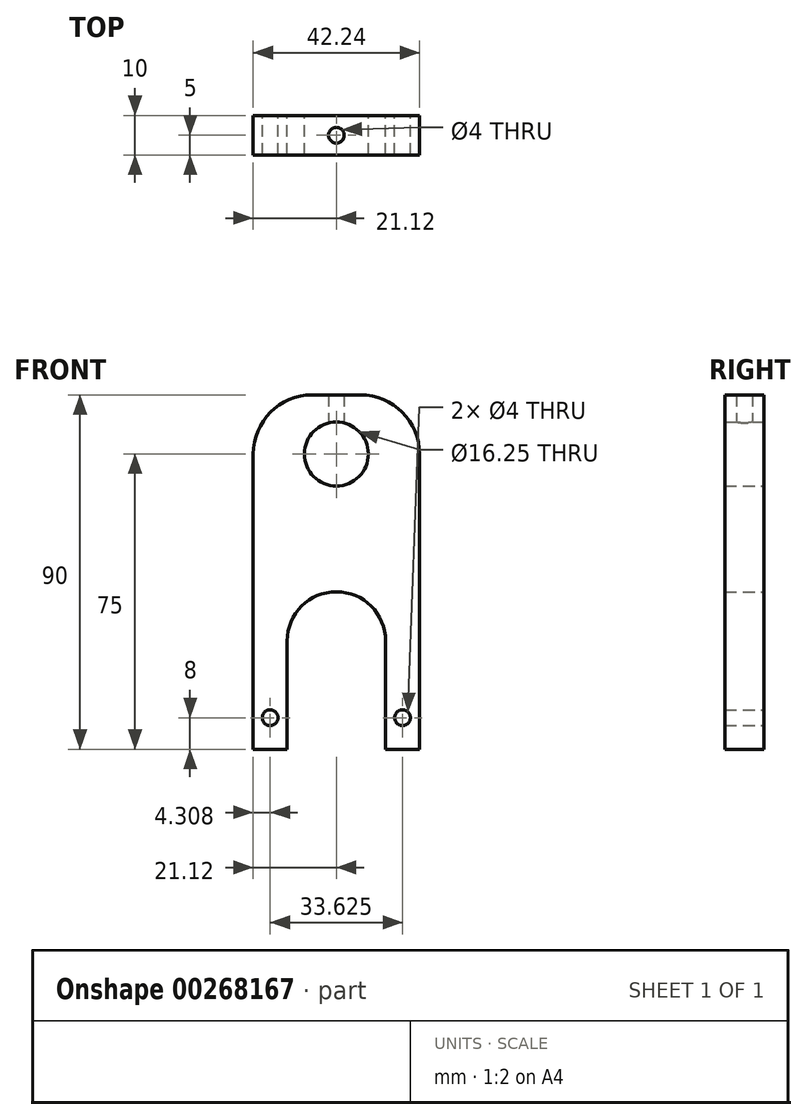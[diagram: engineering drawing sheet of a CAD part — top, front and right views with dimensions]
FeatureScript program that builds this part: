
annotation { "Feature Type Name" : "Feature", "Feature Type Description" : "" }
export const myFeature = defineFeature(function(context is Context, id is Id, definition is map)
    precondition{}
    {
        {
            var Q0;
            Q0=qCreatedBy(makeId("Front.planeOp"),FACE);
            var sketch = newSketch(context, id + "F0", { "sketchPlane" : qUnion([Q0])});
            skLineSegment(sketch, "E0.bottom", {"start": v(6.12, 62.5) * mm, "end": v(-6.13, 62.5) * mm});
            skLineSegment(sketch, "E0.top", {"start": v(21.12, -27.5) * mm, "end": v(12.5, -27.5) * mm});
            skLineSegment(sketch, "E0.left", {"start": v(21.12, 47.5) * mm, "end": v(21.12, -27.5) * mm});
            skLineSegment(sketch, "E0.right", {"start": v(-21.13, 47.5) * mm, "end": v(-21.12, -27.5) * mm});
            skPoint(sketch, "E0.middle", {"position": v(0, 17.5) * mm});
            skLineSegment(sketch, "E1", {"start": v(-12.5, 0) * mm, "end": v(-12.5, -27.5) * mm});
            skLineSegment(sketch, "E2", {"start": v(12.5, 0) * mm, "end": v(12.5, -27.5) * mm});
            skLineSegment(sketch, "E3", {"start": v(-12.5, -27.5) * mm, "end": v(-12.5, -27.5) * mm});
            skLineSegment(sketch, "E4", {"start": v(12.5, -27.5) * mm, "end": v(-12.5, -27.5) * mm, "construction": true});
            skArc(sketch, "E5", {"start": v(-12.5, 0) * mm, "mid": v(0, -12.5) * mm, "end": v(12.5, 0) * mm, "construction": true});
            skArc(sketch, "E6", {"start": v(12.5, 0) * mm, "mid": v(0, 12.5) * mm, "end": v(-12.5, 0) * mm});
            skLineSegment(sketch, "E7", {"start": v(-12.5, -27.5) * mm, "end": v(-21.12, -27.5) * mm});
            skCircle(sketch, "E8", {"center": v(0, 47.5) * mm, "radius": 8.12 * mm});
            skCircle(sketch, "E9", {"center": v(-16.81, -19.5) * mm, "radius": 2 * mm});
            skCircle(sketch, "E10", {"center": v(16.81, -19.5) * mm, "radius": 2 * mm});
            skPoint(sketch, "E11", {"position": v(-16.81, -27.5) * mm});
            skPoint(sketch, "E12", {"position": v(16.81, -27.5) * mm});
            skPoint(sketch, "E13.visualSharp", {"position": v(-21.13, 62.5) * mm});
            skArc(sketch, "E13.filletArc", {"start": v(-6.13, 62.5) * mm, "mid": v(-16.73, 58.1) * mm, "end": v(-21.13, 47.5) * mm});
            skPoint(sketch, "E14.visualSharp", {"position": v(21.12, 62.5) * mm});
            skArc(sketch, "E14.filletArc", {"start": v(21.12, 47.5) * mm, "mid": v(16.73, 58.1) * mm, "end": v(6.13, 62.5) * mm});
            skSolve(sketch);
        }
        {
            var Q0;
            Q0=qCreatedBy(makeId("Top.planeOp"),FACE);
            var sketch = newSketch(context, id + "F1", { "sketchPlane" : qUnion([Q0])});
            skCircle(sketch, "E15", {"center": v(0, 0) * mm, "radius": 2 * mm});
            skCircle(sketch, "E16", {"center": v(-16.81, 0) * mm, "radius": 2 * mm});
            skCircle(sketch, "E17", {"center": v(16.81, 0) * mm, "radius": 2 * mm});
            skLineSegment(sketch, "E18", {"start": v(-21.12, 0) * mm, "end": v(-12.5, 0) * mm, "construction": true});
            skLineSegment(sketch, "E19", {"start": v(12.5, 0) * mm, "end": v(21.12, 0) * mm, "construction": true});
            skSolve(sketch);
        }
        {
            var Q0;
            Q0=makeQuery(id+"F0.imprint","IMPRINT",FACE,{"disambiguationData":[TD([[makeQuery(id+"F0.imprint","IMPRINT",EDGE,{"derivedFrom":sQuery(id+"F0.wireOp",EDGE,"E0.bottom")}),1.0]])]});
            extrude(context, id + "F2", {"entities" : qUnion([Q0]), "endBound" : BoundingType.SYMMETRIC, "depth" : 10 * mm});
        }
        {
            var Q0;
            Q0=makeQuery(id+"F1.imprint","IMPRINT",FACE,{"disambiguationData":[TD([[makeQuery(id+"F1.imprint","IMPRINT",EDGE,{"derivedFrom":sQuery(id+"F1.wireOp",EDGE,"E15")}),1.0]])]});
            extrude(context, id + "F3", {"entities" : qUnion([Q0]), "operationType" : NewBodyOperationType.REMOVE, "endBound" : BoundingType.THROUGH_ALL, "depth" : 87.5 * mm, "hasSecondDirection" : true, "secondDirectionOppositeDirection" : false, "secondDirectionDepth" : 55 * mm});
        }
    });
